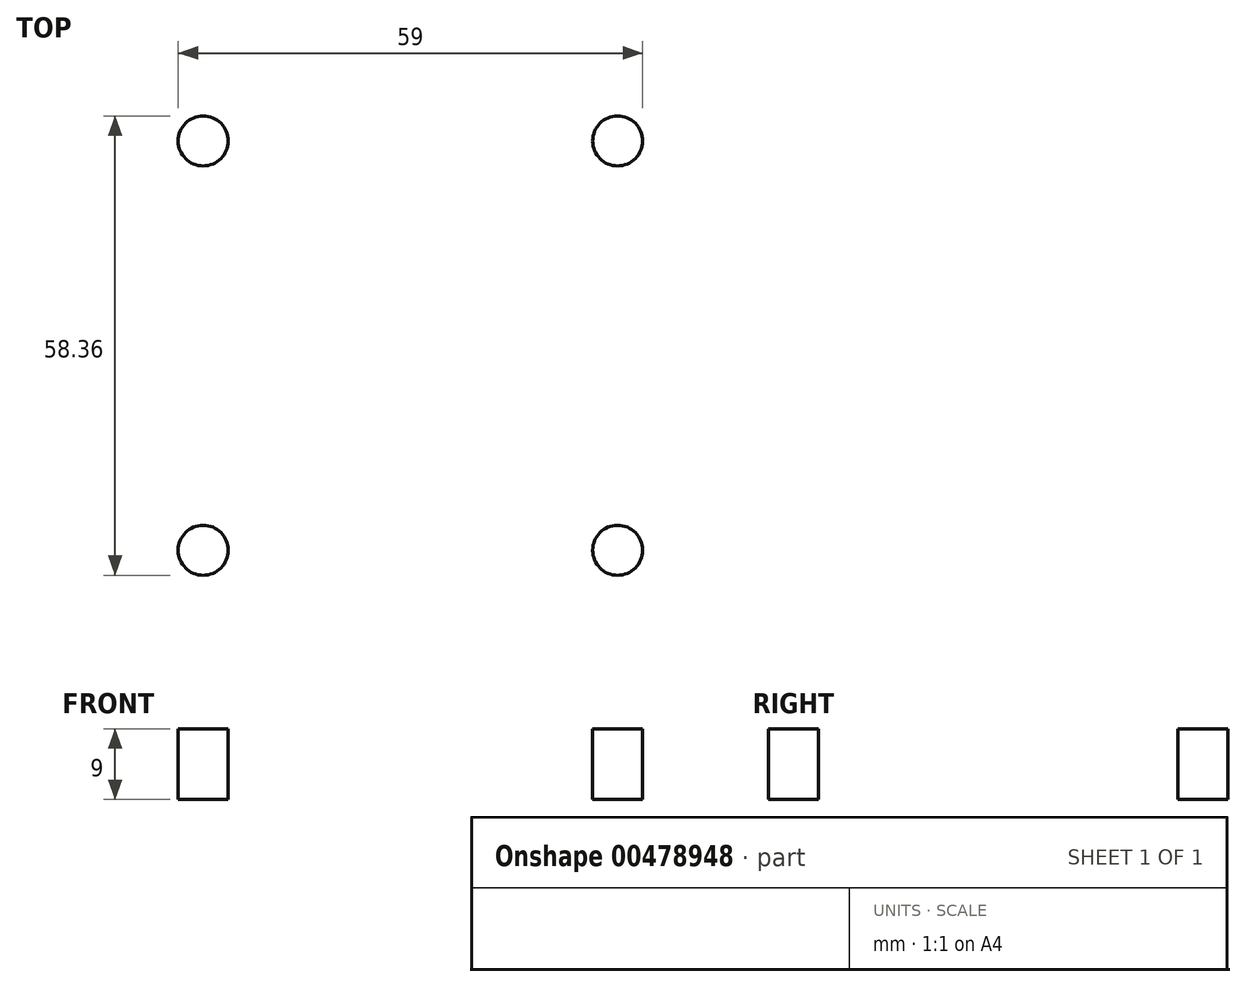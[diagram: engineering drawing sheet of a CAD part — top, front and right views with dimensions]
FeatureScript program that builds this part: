
annotation { "Feature Type Name" : "Feature", "Feature Type Description" : "" }
export const myFeature = defineFeature(function(context is Context, id is Id, definition is map)
    precondition{}
    {
        {
            var Q0;
            Q0=qCreatedBy(makeId("Top.planeOp"),FACE);
            var sketch = newSketch(context, id + "F0", { "sketchPlane" : qUnion([Q0])});
            skLineSegment(sketch, "E0", {"start": v(0, 60) * mm, "end": v(0, -60) * mm});
            skLineSegment(sketch, "E1", {"start": v(-70, 0) * mm, "end": v(70, 0) * mm});
            skLineSegment(sketch, "E2", {"start": v(-31, 37.5) * mm, "end": v(31, 37.5) * mm});
            skLineSegment(sketch, "E3", {"start": v(-31, -37.5) * mm, "end": v(31, -37.5) * mm});
            skCircle(sketch, "E4", {"center": v(-26.32, 26) * mm, "radius": 3.17 * mm});
            skCircle(sketch, "E5", {"center": v(-26.32, -26) * mm, "radius": 3.17 * mm});
            skCircle(sketch, "E6", {"center": v(26.32, -26) * mm, "radius": 3.17 * mm});
            skCircle(sketch, "E7", {"center": v(26.32, 26) * mm, "radius": 3.17 * mm});
            skCircle(sketch, "E8", {"center": v(-41, 0) * mm, "radius": 5.17 * mm});
            skCircle(sketch, "E9", {"center": v(41, 0) * mm, "radius": 5.17 * mm});
            skCircle(sketch, "E10", {"center": v(35, -11) * mm, "radius": 3.5 * mm});
            skLineSegment(sketch, "E11", {"start": v(-55, 12.5) * mm, "end": v(-55, -12.5) * mm});
            skLineSegment(sketch, "E12", {"start": v(55, 12.5) * mm, "end": v(55, -12.5) * mm});
            skCircle(sketch, "E13", {"center": v(0, 22.5) * mm, "radius": 3.17 * mm});
            skCircle(sketch, "E14", {"center": v(22.5, 0) * mm, "radius": 3.17 * mm});
            skCircle(sketch, "E15", {"center": v(0, -22.5) * mm, "radius": 3.17 * mm});
            skCircle(sketch, "E16", {"center": v(-22.5, 0) * mm, "radius": 3.17 * mm});
            skLineSegment(sketch, "E17", {"start": v(-40, 28.5) * mm, "end": v(-40, 27.5) * mm});
            skLineSegment(sketch, "E18", {"start": v(40, 28.5) * mm, "end": v(40, 27.5) * mm});
            skLineSegment(sketch, "E19", {"start": v(-40, -27.5) * mm, "end": v(-40, -28.5) * mm});
            skLineSegment(sketch, "E20", {"start": v(40, -27.5) * mm, "end": v(40, -28.5) * mm});
            skArc(sketch, "E21", {"start": v(-54, 13.5) * mm, "mid": v(-44.1, 17.6) * mm, "end": v(-40, 27.5) * mm});
            skArc(sketch, "E22", {"start": v(-40, -27.5) * mm, "mid": v(-44.1, -17.6) * mm, "end": v(-54, -13.5) * mm});
            skArc(sketch, "E23", {"start": v(54, -13.5) * mm, "mid": v(44.1, -17.6) * mm, "end": v(40, -27.5) * mm});
            skArc(sketch, "E24", {"start": v(40, 27.5) * mm, "mid": v(44.1, 17.6) * mm, "end": v(54, 13.5) * mm});
            skArc(sketch, "E25", {"start": v(-54, 13.5) * mm, "mid": v(-54.7, 13.2) * mm, "end": v(-55, 12.5) * mm});
            skArc(sketch, "E26", {"start": v(-55, -12.5) * mm, "mid": v(-54.7, -13.2) * mm, "end": v(-54, -13.5) * mm});
            skArc(sketch, "E27", {"start": v(55, 12.5) * mm, "mid": v(54.7, 13.2) * mm, "end": v(54, 13.5) * mm});
            skArc(sketch, "E28", {"start": v(54, -13.5) * mm, "mid": v(54.7, -13.2) * mm, "end": v(55, -12.5) * mm});
            skArc(sketch, "E29", {"start": v(-31, 37.5) * mm, "mid": v(-37.36, 34.86) * mm, "end": v(-40, 28.5) * mm});
            skArc(sketch, "E30", {"start": v(40, 28.5) * mm, "mid": v(37.36, 34.86) * mm, "end": v(31, 37.5) * mm});
            skArc(sketch, "E31", {"start": v(31, -37.5) * mm, "mid": v(37.36, -34.86) * mm, "end": v(40, -28.5) * mm});
            skArc(sketch, "E32", {"start": v(-40, -28.5) * mm, "mid": v(-37.36, -34.86) * mm, "end": v(-31, -37.5) * mm});
            skCircle(sketch, "E33", {"center": v(0, 0) * mm, "radius": 11.5 * mm});
            skArc(sketch, "E34", {"start": v(-41.3, -11.6) * mm, "mid": v(-34.97, -9.91) * mm, "end": v(-30.57, -5.07) * mm});
            skArc(sketch, "E35", {"start": v(-30.57, -5.07) * mm, "mid": v(-23.94, -9.42) * mm, "end": v(-16.31, -7.24) * mm});
            skArc(sketch, "E36", {"start": v(-16.31, -7.24) * mm, "mid": v(-12.62, -12.62) * mm, "end": v(-7.24, -16.31) * mm});
            skArc(sketch, "E37", {"start": v(16.31, -7.24) * mm, "mid": v(20.59, -9.33) * mm, "end": v(25.34, -9.1) * mm});
            skArc(sketch, "E38", {"start": v(25.34, -9.1) * mm, "mid": v(25.34, -12.94) * mm, "end": v(26.82, -16.49) * mm});
            skArc(sketch, "E39", {"start": v(26.82, -16.49) * mm, "mid": v(18.09, -21.22) * mm, "end": v(18.31, -31.15) * mm});
            skArc(sketch, "E40", {"start": v(-7.24, -16.31) * mm, "mid": v(-9.3, -24.54) * mm, "end": v(-3.99, -31.15) * mm});
            skArc(sketch, "E41", {"start": v(-18.31, -31.15) * mm, "mid": v(-21.4, -17.85) * mm, "end": v(-34.61, -21.3) * mm});
            skLineSegment(sketch, "E42", {"start": v(-18.31, -31.15) * mm, "end": v(-3.99, -31.15) * mm});
            skArc(sketch, "E43", {"start": v(-34.61, -21.3) * mm, "mid": v(-37.24, -15.96) * mm, "end": v(-41.3, -11.6) * mm});
            skArc(sketch, "E44", {"start": v(-41.3, 11.6) * mm, "mid": v(-37.24, 15.96) * mm, "end": v(-34.61, 21.3) * mm});
            skArc(sketch, "E45", {"start": v(-30.57, 5.07) * mm, "mid": v(-34.97, 9.91) * mm, "end": v(-41.3, 11.6) * mm});
            skArc(sketch, "E46", {"start": v(-16.31, 7.24) * mm, "mid": v(-23.94, 9.42) * mm, "end": v(-30.57, 5.07) * mm});
            skArc(sketch, "E47", {"start": v(3.99, -31.15) * mm, "mid": v(9.3, -24.54) * mm, "end": v(7.24, -16.31) * mm});
            skLineSegment(sketch, "E48", {"start": v(3.99, -31.15) * mm, "end": v(18.31, -31.15) * mm});
            skArc(sketch, "E49", {"start": v(7.24, -16.31) * mm, "mid": v(12.62, -12.62) * mm, "end": v(16.31, -7.24) * mm});
            skArc(sketch, "E50", {"start": v(16.31, 7.24) * mm, "mid": v(12.62, 12.62) * mm, "end": v(7.24, 16.31) * mm});
            skArc(sketch, "E51", {"start": v(-34.61, 21.3) * mm, "mid": v(-21.4, 17.85) * mm, "end": v(-18.31, 31.15) * mm});
            skLineSegment(sketch, "E52", {"start": v(-18.31, 31.15) * mm, "end": v(-3.99, 31.15) * mm});
            skArc(sketch, "E53", {"start": v(-3.99, 31.15) * mm, "mid": v(-9.3, 24.54) * mm, "end": v(-7.24, 16.31) * mm});
            skArc(sketch, "E54", {"start": v(7.24, 16.31) * mm, "mid": v(9.3, 24.54) * mm, "end": v(3.99, 31.15) * mm});
            skLineSegment(sketch, "E55", {"start": v(3.99, 31.15) * mm, "end": v(18.31, 31.15) * mm});
            skArc(sketch, "E56", {"start": v(18.31, 31.15) * mm, "mid": v(21.4, 17.85) * mm, "end": v(34.61, 21.3) * mm});
            skArc(sketch, "E57", {"start": v(34.61, 21.3) * mm, "mid": v(37.24, 15.96) * mm, "end": v(41.3, 11.6) * mm});
            skArc(sketch, "E58", {"start": v(-7.24, 16.31) * mm, "mid": v(-12.62, 12.62) * mm, "end": v(-16.31, 7.24) * mm});
            skArc(sketch, "E59", {"start": v(30.57, 5.07) * mm, "mid": v(23.94, 9.42) * mm, "end": v(16.31, 7.24) * mm});
            skArc(sketch, "E60", {"start": v(41.3, 11.6) * mm, "mid": v(34.97, 9.91) * mm, "end": v(30.57, 5.07) * mm});
            skSolve(sketch);
        }
        {
            var Q0;
            Q0=makeQuery(id+"F0.imprint","IMPRINT",FACE,{"disambiguationData":[TD([[makeQuery(id+"F0.imprint","IMPRINT",EDGE,{"derivedFrom":sQuery(id+"F0.wireOp",EDGE,"E4")}),1.0]])]});
            var Q1;
            Q1=makeQuery(id+"F0.imprint","IMPRINT",FACE,{"disambiguationData":[TD([[makeQuery(id+"F0.imprint","IMPRINT",EDGE,{"derivedFrom":sQuery(id+"F0.wireOp",EDGE,"E5")}),1.0]])]});
            var Q2;
            Q2=makeQuery(id+"F0.imprint","IMPRINT",FACE,{"disambiguationData":[TD([[makeQuery(id+"F0.imprint","IMPRINT",EDGE,{"derivedFrom":sQuery(id+"F0.wireOp",EDGE,"E6")}),1.0]])]});
            var Q3;
            Q3=makeQuery(id+"F0.imprint","IMPRINT",FACE,{"disambiguationData":[TD([[makeQuery(id+"F0.imprint","IMPRINT",EDGE,{"derivedFrom":sQuery(id+"F0.wireOp",EDGE,"E7")}),1.0]])]});
            extrude(context, id + "F1", {"entities" : qUnion([Q0, Q1, Q2, Q3]), "depth" : 9 * mm});
        }
    });
